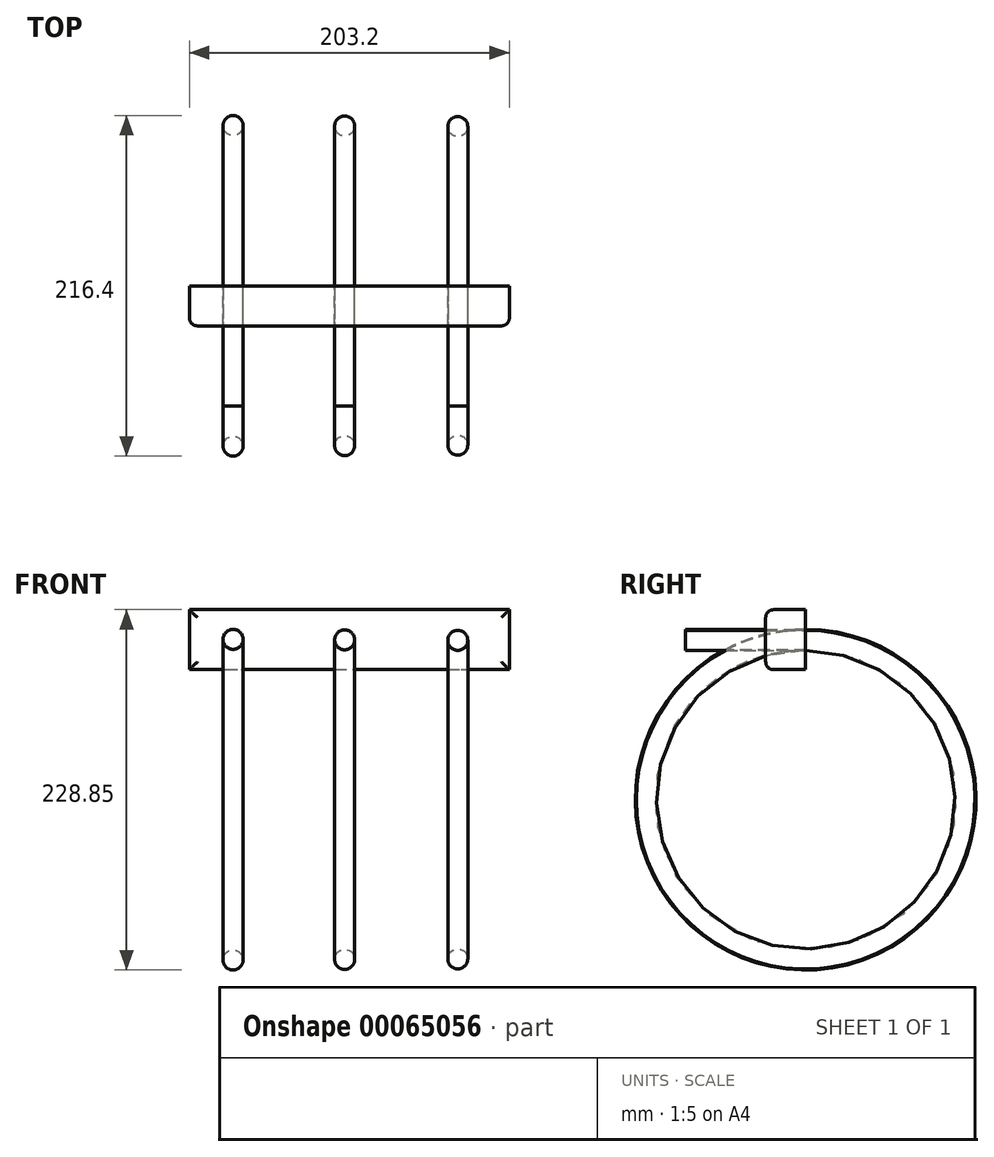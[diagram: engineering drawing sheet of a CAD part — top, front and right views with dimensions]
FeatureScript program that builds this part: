
annotation { "Feature Type Name" : "Feature", "Feature Type Description" : "" }
export const myFeature = defineFeature(function(context is Context, id is Id, definition is map)
    precondition{}
    {
        {
            var Q0;
            Q0=qCreatedBy(makeId("Front.planeOp"),FACE);
            var sketch = newSketch(context, id + "F0", { "sketchPlane" : qUnion([Q0])});
            skLineSegment(sketch, "E0.bottom", {"start": v(-39.18, 120.65) * mm, "end": v(164.02, 120.65) * mm});
            skLineSegment(sketch, "E0.top", {"start": v(-39.18, 82.55) * mm, "end": v(164.02, 82.55) * mm});
            skLineSegment(sketch, "E0.left", {"start": v(-39.18, 120.65) * mm, "end": v(-39.18, 82.55) * mm});
            skLineSegment(sketch, "E0.right", {"start": v(164.02, 120.65) * mm, "end": v(164.02, 82.55) * mm});
            skLineSegment(sketch, "E1", {"start": v(-75.67, 0) * mm, "end": v(76.87, 0) * mm, "construction": true});
            skLineSegment(sketch, "E2", {"start": v(-39.18, 101.6) * mm, "end": v(197.8, 101.6) * mm, "construction": true});
            skLineSegment(sketch, "E3", {"start": v(-39.18, 101.6) * mm, "end": v(-39.18, 0) * mm, "construction": true});
            skSolve(sketch);
        }
        {
            var Q0;
            Q0=makeQuery(id+"F0.imprint","IMPRINT",FACE,{"disambiguationData":[TD([[makeQuery(id+"F0.imprint","IMPRINT",EDGE,{"derivedFrom":sQuery(id+"F0.wireOp",EDGE,"E0.bottom")}),-1.0]])]});
            var sketch = newSketch(context, id + "F1", { "sketchPlane" : qUnion([Q0])});
            skCircle(sketch, "E4", {"center": v(-11.44, 101.85) * mm, "radius": 6.35 * mm});
            skCircle(sketch, "E5", {"center": v(59.4, 101.51) * mm, "radius": 6.35 * mm});
            skCircle(sketch, "E6", {"center": v(131.26, 101.18) * mm, "radius": 6.35 * mm});
            skSolve(sketch);
        }
        {
            var Q0;
            Q0 = qSketchRegion(id + "F1", true);
            var Q1;
            Q1=sQuery(id+"F0.wireOp",EDGE,"E1");
            revolve(context, id + "F2", {"entities" : qUnion([Q0]), "axis" : qUnion([Q1]), "revolveType" : RevolveType.FULL});
        }
        {
            var Q0;
            Q0 = qSketchRegion(id + "F1", true);
            extrude(context, id + "F3", {"entities" : qUnion([Q0]), "depth" : 76.2 * mm});
        }
        {
            var Q0;
            Q0 = qSketchRegion(id + "F0", true);
            extrude(context, id + "F4", {"entities" : qUnion([Q0]), "depth" : 25.4 * mm});
        }
        {
            var Q0;
            Q0=makeQuery(id+"F4.opExtrude","CAP_FACE",FACE,{"disambiguationData":[OSD([sQuery(id+"F0.wireOp",EDGE,"E0.bottom"),sQuery(id+"F0.wireOp",EDGE,"E0.top"),sQuery(id+"F0.wireOp",EDGE,"E0.left"),sQuery(id+"F0.wireOp",EDGE,"E0.right")])],"isStart":false});
            fillet(context, id + "F5", {"entities" : qUnion([Q0]), "radius" : 5.08 * mm, "tangentPropagation" : true, "allowEdgeOverflow" : false});
        }
    });
